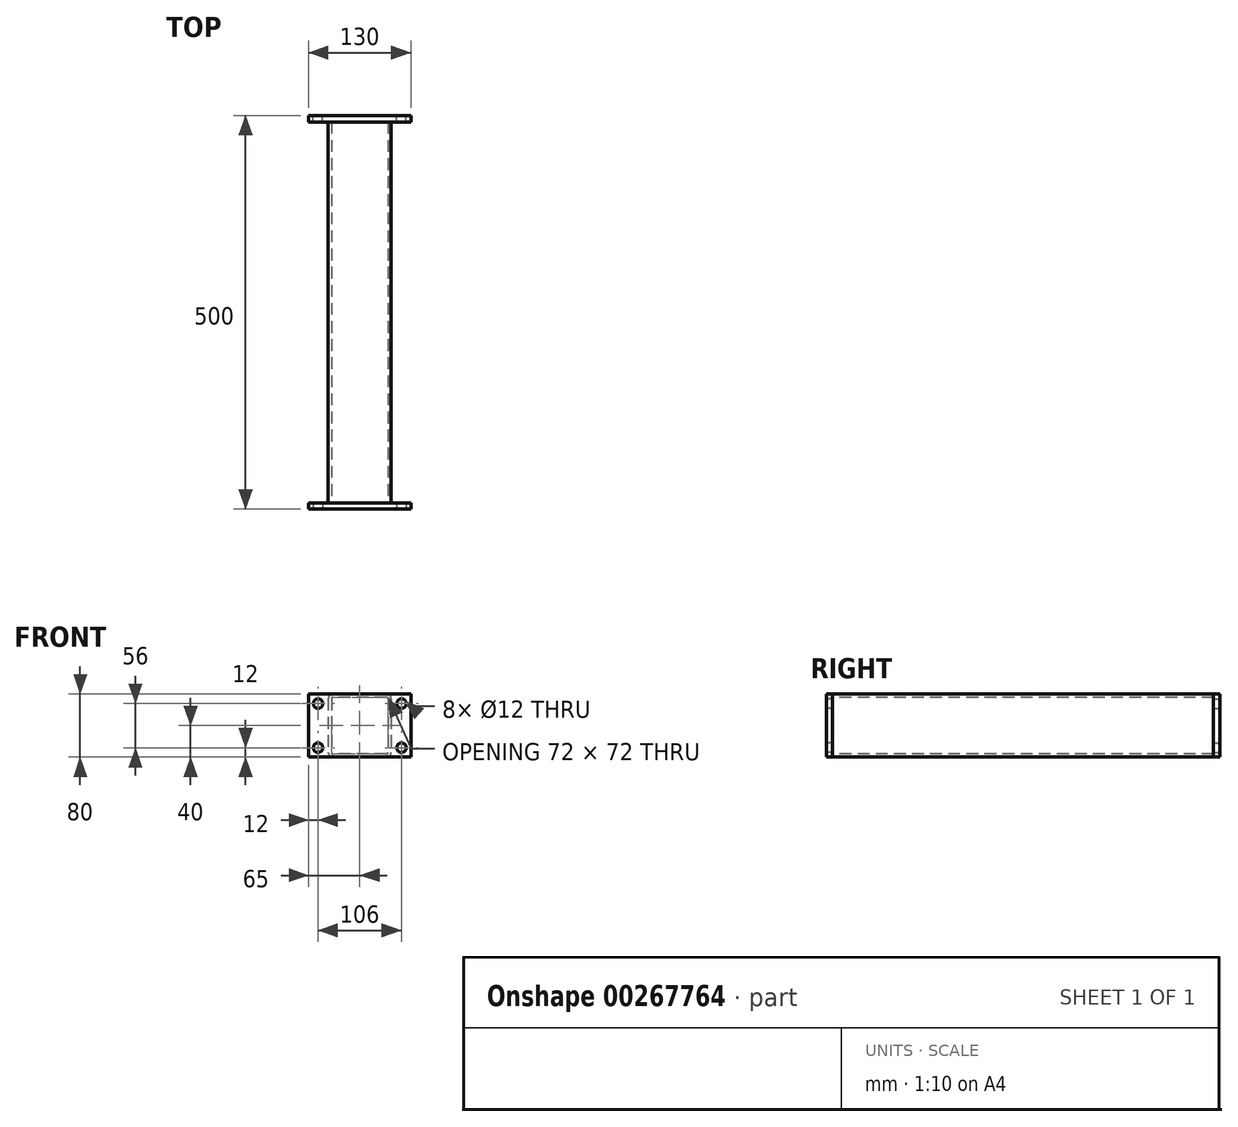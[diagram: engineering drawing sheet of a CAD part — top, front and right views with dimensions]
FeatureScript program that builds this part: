
annotation { "Feature Type Name" : "Feature", "Feature Type Description" : "" }
export const myFeature = defineFeature(function(context is Context, id is Id, definition is map)
    precondition{}
    {
        {
            var Q0;
            Q0=qCreatedBy(makeId("Front.planeOp"),FACE);
            var sketch = newSketch(context, id + "F0", { "sketchPlane" : qUnion([Q0])});
            skLineSegment(sketch, "E0.bottom", {"start": v(34, 40) * mm, "end": v(-34, 40) * mm});
            skLineSegment(sketch, "E0.top", {"start": v(34, -40) * mm, "end": v(-34, -40) * mm});
            skLineSegment(sketch, "E0.left", {"start": v(40, 34) * mm, "end": v(40, -34) * mm});
            skLineSegment(sketch, "E0.right", {"start": v(-40, 34) * mm, "end": v(-40, -34) * mm});
            skPoint(sketch, "E0.middle", {"position": v(0, 0) * mm});
            skPoint(sketch, "E1.visualSharp", {"position": v(-40, 40) * mm});
            skArc(sketch, "E1.filletArc", {"start": v(-34, 40) * mm, "mid": v(-38.24, 38.24) * mm, "end": v(-40, 34) * mm});
            skPoint(sketch, "E2.visualSharp", {"position": v(40, 40) * mm});
            skArc(sketch, "E2.filletArc", {"start": v(40, 34) * mm, "mid": v(38.24, 38.24) * mm, "end": v(34, 40) * mm});
            skPoint(sketch, "E3.visualSharp", {"position": v(40, -40) * mm});
            skArc(sketch, "E3.filletArc", {"start": v(34, -40) * mm, "mid": v(38.24, -38.24) * mm, "end": v(40, -34) * mm});
            skPoint(sketch, "E4.visualSharp", {"position": v(-40, -40) * mm});
            skArc(sketch, "E4.filletArc", {"start": v(-40, -34) * mm, "mid": v(-38.24, -38.24) * mm, "end": v(-34, -40) * mm});
            skArc(sketch, "E5.0", {"start": v(-34, 36) * mm, "mid": v(-35.41, 35.41) * mm, "end": v(-36, 34) * mm});
            skLineSegment(sketch, "E5.1", {"start": v(34, 36) * mm, "end": v(-34, 36) * mm});
            skLineSegment(sketch, "E5.2", {"start": v(-36, 34) * mm, "end": v(-36, -34) * mm});
            skArc(sketch, "E5.3", {"start": v(36, 34) * mm, "mid": v(35.41, 35.41) * mm, "end": v(34, 36) * mm});
            skArc(sketch, "E5.4", {"start": v(-36, -34) * mm, "mid": v(-35.41, -35.41) * mm, "end": v(-34, -36) * mm});
            skLineSegment(sketch, "E5.5", {"start": v(34, -36) * mm, "end": v(-34, -36) * mm});
            skArc(sketch, "E5.6", {"start": v(34, -36) * mm, "mid": v(35.41, -35.41) * mm, "end": v(36, -34) * mm});
            skLineSegment(sketch, "E5.7", {"start": v(36, 34) * mm, "end": v(36, -34) * mm});
            skSolve(sketch);
        }
        {
            var Q0;
            Q0=makeQuery(id+"F0.imprint","IMPRINT",FACE,{"disambiguationData":[TD([[makeQuery(id+"F0.imprint","IMPRINT",EDGE,{"derivedFrom":sQuery(id+"F0.wireOp",EDGE,"E0.bottom")}),1.0]])]});
            extrude(context, id + "F1", {"entities" : qUnion([Q0]), "oppositeDirection" : true, "depth" : 484 * mm});
        }
        {
            var Q0;
            Q0=qCreatedBy(makeId("Front.planeOp"),FACE);
            cPlane(context, id + "F2", {"entities" : qUnion([Q0]), "cplaneType" : CPlaneType.OFFSET, "offset" : 8 * mm, "width" : 150 * mm, "height" : 150 * mm});
        }
        {
            var Q0;
            Q0=qCreatedBy(id+"F2.planeOp",FACE);
            var sketch = newSketch(context, id + "F3", { "sketchPlane" : qUnion([Q0])});
            skLineSegment(sketch, "E6.bottom", {"start": v(-65, 40) * mm, "end": v(65, 40) * mm});
            skLineSegment(sketch, "E6.top", {"start": v(-65, -40) * mm, "end": v(65, -40) * mm});
            skLineSegment(sketch, "E6.left", {"start": v(-65, 40) * mm, "end": v(-65, -40) * mm});
            skLineSegment(sketch, "E6.right", {"start": v(65, 40) * mm, "end": v(65, -40) * mm});
            skPoint(sketch, "E6.middle", {"position": v(0, 0) * mm});
            skCircle(sketch, "E7", {"center": v(-53, 28) * mm, "radius": 6 * mm});
            skCircle(sketch, "E8", {"center": v(-53, -28) * mm, "radius": 6 * mm});
            skCircle(sketch, "E9", {"center": v(53, -28) * mm, "radius": 6 * mm});
            skCircle(sketch, "E10", {"center": v(53, 28) * mm, "radius": 6 * mm});
            skSolve(sketch);
        }
        {
            var Q0;
            Q0=makeQuery(id+"F3.imprint","IMPRINT",FACE,{"disambiguationData":[TD([[makeQuery(id+"F3.imprint","IMPRINT",EDGE,{"derivedFrom":sQuery(id+"F3.wireOp",EDGE,"E6.bottom")}),-1.0]])]});
            extrude(context, id + "F4", {"entities" : qUnion([Q0]), "oppositeDirection" : true, "depth" : 8 * mm});
        }
        {
            var Q0;
            Q0=makeQuery(id+"F1.opExtrude","CAP_FACE",FACE,{"disambiguationData":[OSD([sQuery(id+"F0.wireOp",EDGE,"E0.bottom"),sQuery(id+"F0.wireOp",EDGE,"E0.top"),sQuery(id+"F0.wireOp",EDGE,"E0.left"),sQuery(id+"F0.wireOp",EDGE,"E0.right"),sQuery(id+"F0.wireOp",EDGE,"E1.filletArc"),sQuery(id+"F0.wireOp",EDGE,"E2.filletArc"),sQuery(id+"F0.wireOp",EDGE,"E3.filletArc"),sQuery(id+"F0.wireOp",EDGE,"E4.filletArc"),sQuery(id+"F0.wireOp",EDGE,"E5.0"),sQuery(id+"F0.wireOp",EDGE,"E5.1"),sQuery(id+"F0.wireOp",EDGE,"E5.2"),sQuery(id+"F0.wireOp",EDGE,"E5.3"),sQuery(id+"F0.wireOp",EDGE,"E5.4"),sQuery(id+"F0.wireOp",EDGE,"E5.5"),sQuery(id+"F0.wireOp",EDGE,"E5.6"),sQuery(id+"F0.wireOp",EDGE,"E5.7")])],"isStart":false});
            cPlane(context, id + "F5", {"entities" : qUnion([Q0]), "cplaneType" : CPlaneType.OFFSET, "offset" : 8 * mm, "width" : 150 * mm, "height" : 150 * mm});
        }
        {
            var Q0;
            Q0=qCreatedBy(id+"F5.planeOp",FACE);
            var sketch = newSketch(context, id + "F6", { "sketchPlane" : qUnion([Q0])});
            skLineSegment(sketch, "E11.bottom", {"start": v(-65, 40) * mm, "end": v(65, 40) * mm});
            skLineSegment(sketch, "E11.top", {"start": v(-65, -40) * mm, "end": v(65, -40) * mm});
            skLineSegment(sketch, "E11.left", {"start": v(-65, 40) * mm, "end": v(-65, -40) * mm});
            skLineSegment(sketch, "E11.right", {"start": v(65, 40) * mm, "end": v(65, -40) * mm});
            skPoint(sketch, "E11.middle", {"position": v(0, 0) * mm});
            skCircle(sketch, "E12", {"center": v(-53, 28) * mm, "radius": 6 * mm});
            skCircle(sketch, "E13", {"center": v(-53, -28) * mm, "radius": 6 * mm});
            skCircle(sketch, "E14", {"center": v(53, -28) * mm, "radius": 6 * mm});
            skCircle(sketch, "E15", {"center": v(53, 28) * mm, "radius": 6 * mm});
            skSolve(sketch);
        }
        {
            var Q0;
            Q0=makeQuery(id+"F6.imprint","IMPRINT",FACE,{"disambiguationData":[TD([[makeQuery(id+"F6.imprint","IMPRINT",EDGE,{"derivedFrom":sQuery(id+"F6.wireOp",EDGE,"E11.bottom")}),-1.0]])]});
            extrude(context, id + "F7", {"entities" : qUnion([Q0]), "oppositeDirection" : true, "depth" : 8 * mm});
        }
    });
